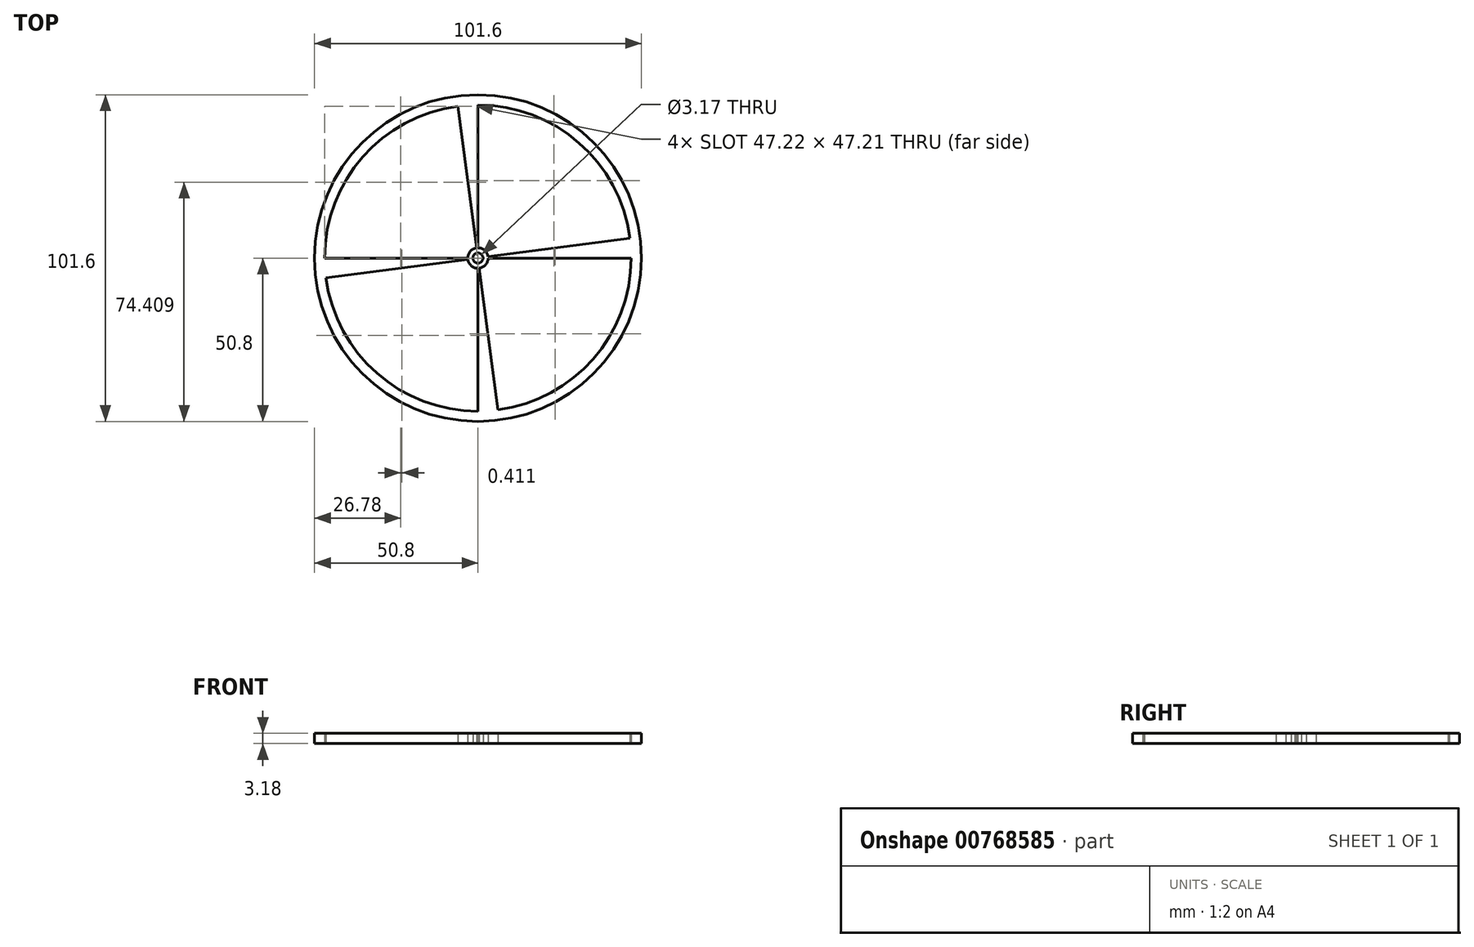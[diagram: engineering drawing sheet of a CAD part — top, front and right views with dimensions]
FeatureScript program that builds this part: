
annotation { "Feature Type Name" : "Feature", "Feature Type Description" : "" }
export const myFeature = defineFeature(function(context is Context, id is Id, definition is map)
    precondition{}
    {
        {
            var Q0;
            Q0=qCreatedBy(makeId("Top.planeOp"),FACE);
            var sketch = newSketch(context, id + "F0", { "sketchPlane" : qUnion([Q0])});
            skCircle(sketch, "E0", {"center": v(0, 0) * mm, "radius": 1.59 * mm});
            skCircle(sketch, "E1", {"center": v(0, 0) * mm, "radius": 50.8 * mm});
            skLineSegment(sketch, "E2", {"start": v(0, 0) * mm, "end": v(0, 50.8) * mm});
            skLineSegment(sketch, "E3", {"start": v(0, 0) * mm, "end": v(0, -50.8) * mm});
            skLineSegment(sketch, "E4", {"start": v(0, 0) * mm, "end": v(50.8, 0) * mm});
            skLineSegment(sketch, "E5", {"start": v(0, 0) * mm, "end": v(-50.8, 0) * mm});
            skLineSegment(sketch, "E6", {"start": v(0, 0) * mm, "end": v(-6.63, 50.37) * mm});
            skLineSegment(sketch, "E7", {"start": v(0, 0) * mm, "end": v(6.63, -50.37) * mm});
            skLineSegment(sketch, "E8", {"start": v(0, 0) * mm, "end": v(-50.37, -6.63) * mm});
            skLineSegment(sketch, "E9", {"start": v(0, 0) * mm, "end": v(50.37, 6.63) * mm});
            skCircle(sketch, "E10", {"center": v(0, 0) * mm, "radius": 47.63 * mm});
            skCircle(sketch, "E11", {"center": v(0, 0) * mm, "radius": 3.18 * mm});
            skSolve(sketch);
        }
        {
            var Q0;
            {var subQ0=sQuery(id+"F0.wireOp",EDGE,"E5");var subQ1=sQuery(id+"F0.wireOp",EDGE,"E1");var subQ2=makeQuery(id+"F0.imprint","INTERSECT",VERTEX,{"derivedFrom":[subQ1,subQ0]});Q0=makeQuery(id+"F0.imprint","IMPRINT",FACE,{"disambiguationData":[TD([[makeQuery(id+"F0.imprint","IMPRINT",EDGE,{"disambiguationData":[TD([[subQ2,1.0]])],"derivedFrom":subQ1}),1.0]])]});}
            var Q1;
            {var subQ0=sQuery(id+"F0.wireOp",EDGE,"E5");var subQ1=sQuery(id+"F0.wireOp",EDGE,"E1");var subQ2=makeQuery(id+"F0.imprint","INTERSECT",VERTEX,{"derivedFrom":[subQ1,subQ0]});Q1=makeQuery(id+"F0.imprint","IMPRINT",FACE,{"disambiguationData":[TD([[makeQuery(id+"F0.imprint","IMPRINT",EDGE,{"disambiguationData":[TD([[subQ2,-1.0]])],"derivedFrom":subQ1}),1.0]])]});}
            var Q2;
            {var subQ0=sQuery(id+"F0.wireOp",EDGE,"E3");var subQ1=sQuery(id+"F0.wireOp",EDGE,"E1");var subQ2=makeQuery(id+"F0.imprint","INTERSECT",VERTEX,{"derivedFrom":[subQ1,subQ0]});Q2=makeQuery(id+"F0.imprint","IMPRINT",FACE,{"disambiguationData":[TD([[makeQuery(id+"F0.imprint","IMPRINT",EDGE,{"disambiguationData":[TD([[subQ2,1.0]])],"derivedFrom":subQ1}),1.0]])]});}
            var Q3;
            {var subQ0=sQuery(id+"F0.wireOp",EDGE,"E4");var subQ1=sQuery(id+"F0.wireOp",EDGE,"E1");var subQ2=makeQuery(id+"F0.imprint","INTERSECT",VERTEX,{"derivedFrom":[subQ1,subQ0]});Q3=makeQuery(id+"F0.imprint","IMPRINT",FACE,{"disambiguationData":[TD([[makeQuery(id+"F0.imprint","IMPRINT",EDGE,{"disambiguationData":[TD([[subQ2,1.0]])],"derivedFrom":subQ1}),1.0]])]});}
            var Q4;
            {var subQ0=sQuery(id+"F0.wireOp",EDGE,"E2");var subQ1=sQuery(id+"F0.wireOp",EDGE,"E1");var subQ2=makeQuery(id+"F0.imprint","INTERSECT",VERTEX,{"derivedFrom":[subQ1,subQ0]});Q4=makeQuery(id+"F0.imprint","IMPRINT",FACE,{"disambiguationData":[TD([[makeQuery(id+"F0.imprint","IMPRINT",EDGE,{"disambiguationData":[TD([[subQ2,1.0]])],"derivedFrom":subQ1}),1.0]])]});}
            var Q5;
            {var subQ0=sQuery(id+"F0.wireOp",EDGE,"E2");var subQ1=sQuery(id+"F0.wireOp",EDGE,"E1");var subQ2=makeQuery(id+"F0.imprint","INTERSECT",VERTEX,{"derivedFrom":[subQ1,subQ0]});Q5=makeQuery(id+"F0.imprint","IMPRINT",FACE,{"disambiguationData":[TD([[makeQuery(id+"F0.imprint","IMPRINT",EDGE,{"disambiguationData":[TD([[subQ2,-1.0]])],"derivedFrom":subQ1}),1.0]])]});}
            var Q6;
            {var subQ0=sQuery(id+"F0.wireOp",EDGE,"E4");var subQ1=sQuery(id+"F0.wireOp",EDGE,"E1");var subQ2=makeQuery(id+"F0.imprint","INTERSECT",VERTEX,{"derivedFrom":[subQ1,subQ0]});Q6=makeQuery(id+"F0.imprint","IMPRINT",FACE,{"disambiguationData":[TD([[makeQuery(id+"F0.imprint","IMPRINT",EDGE,{"disambiguationData":[TD([[subQ2,-1.0]])],"derivedFrom":subQ1}),1.0]])]});}
            var Q7;
            {var subQ0=sQuery(id+"F0.wireOp",EDGE,"E3");var subQ1=sQuery(id+"F0.wireOp",EDGE,"E1");var subQ2=makeQuery(id+"F0.imprint","INTERSECT",VERTEX,{"derivedFrom":[subQ1,subQ0]});Q7=makeQuery(id+"F0.imprint","IMPRINT",FACE,{"disambiguationData":[TD([[makeQuery(id+"F0.imprint","IMPRINT",EDGE,{"disambiguationData":[TD([[subQ2,-1.0]])],"derivedFrom":subQ1}),1.0]])]});}
            var Q8;
            {var subQ0=sQuery(id+"F0.wireOp",EDGE,"E6");var subQ1=sQuery(id+"F0.wireOp",EDGE,"E0");var subQ2=makeQuery(id+"F0.imprint","INTERSECT",VERTEX,{"derivedFrom":[subQ1,subQ0]});Q8=makeQuery(id+"F0.imprint","IMPRINT",FACE,{"disambiguationData":[TD([[makeQuery(id+"F0.imprint","IMPRINT",EDGE,{"disambiguationData":[TD([[subQ2,-1.0]])],"derivedFrom":subQ1}),-1.0]])]});}
            var Q9;
            {var subQ0=sQuery(id+"F0.wireOp",EDGE,"E5");var subQ1=sQuery(id+"F0.wireOp",EDGE,"E0");var subQ2=makeQuery(id+"F0.imprint","INTERSECT",VERTEX,{"derivedFrom":[subQ1,subQ0]});Q9=makeQuery(id+"F0.imprint","IMPRINT",FACE,{"disambiguationData":[TD([[makeQuery(id+"F0.imprint","IMPRINT",EDGE,{"disambiguationData":[TD([[subQ2,-1.0]])],"derivedFrom":subQ1}),-1.0]])]});}
            var Q10;
            {var subQ0=sQuery(id+"F0.wireOp",EDGE,"E8");var subQ1=sQuery(id+"F0.wireOp",EDGE,"E0");var subQ2=makeQuery(id+"F0.imprint","INTERSECT",VERTEX,{"derivedFrom":[subQ1,subQ0]});Q10=makeQuery(id+"F0.imprint","IMPRINT",FACE,{"disambiguationData":[TD([[makeQuery(id+"F0.imprint","IMPRINT",EDGE,{"disambiguationData":[TD([[subQ2,-1.0]])],"derivedFrom":subQ1}),-1.0]])]});}
            var Q11;
            {var subQ0=sQuery(id+"F0.wireOp",EDGE,"E3");var subQ1=sQuery(id+"F0.wireOp",EDGE,"E0");var subQ2=makeQuery(id+"F0.imprint","INTERSECT",VERTEX,{"derivedFrom":[subQ1,subQ0]});Q11=makeQuery(id+"F0.imprint","IMPRINT",FACE,{"disambiguationData":[TD([[makeQuery(id+"F0.imprint","IMPRINT",EDGE,{"disambiguationData":[TD([[subQ2,-1.0]])],"derivedFrom":subQ1}),-1.0]])]});}
            var Q12;
            {var subQ0=sQuery(id+"F0.wireOp",EDGE,"E4");var subQ1=sQuery(id+"F0.wireOp",EDGE,"E0");var subQ2=makeQuery(id+"F0.imprint","INTERSECT",VERTEX,{"derivedFrom":[subQ1,subQ0]});Q12=makeQuery(id+"F0.imprint","IMPRINT",FACE,{"disambiguationData":[TD([[makeQuery(id+"F0.imprint","IMPRINT",EDGE,{"disambiguationData":[TD([[subQ2,1.0]])],"derivedFrom":subQ1}),-1.0]])]});}
            var Q13;
            {var subQ0=sQuery(id+"F0.wireOp",EDGE,"E9");var subQ1=sQuery(id+"F0.wireOp",EDGE,"E0");var subQ2=makeQuery(id+"F0.imprint","INTERSECT",VERTEX,{"derivedFrom":[subQ1,subQ0]});Q13=makeQuery(id+"F0.imprint","IMPRINT",FACE,{"disambiguationData":[TD([[makeQuery(id+"F0.imprint","IMPRINT",EDGE,{"disambiguationData":[TD([[subQ2,1.0]])],"derivedFrom":subQ1}),-1.0]])]});}
            var Q14;
            {var subQ0=sQuery(id+"F0.wireOp",EDGE,"E9");var subQ1=sQuery(id+"F0.wireOp",EDGE,"E0");var subQ2=makeQuery(id+"F0.imprint","INTERSECT",VERTEX,{"derivedFrom":[subQ1,subQ0]});Q14=makeQuery(id+"F0.imprint","IMPRINT",FACE,{"disambiguationData":[TD([[makeQuery(id+"F0.imprint","IMPRINT",EDGE,{"disambiguationData":[TD([[subQ2,-1.0]])],"derivedFrom":subQ1}),-1.0]])]});}
            var Q15;
            {var subQ0=sQuery(id+"F0.wireOp",EDGE,"E2");var subQ1=sQuery(id+"F0.wireOp",EDGE,"E0");var subQ2=makeQuery(id+"F0.imprint","INTERSECT",VERTEX,{"derivedFrom":[subQ1,subQ0]});Q15=makeQuery(id+"F0.imprint","IMPRINT",FACE,{"disambiguationData":[TD([[makeQuery(id+"F0.imprint","IMPRINT",EDGE,{"disambiguationData":[TD([[subQ2,-1.0]])],"derivedFrom":subQ1}),-1.0]])]});}
            var Q16;
            {var subQ0=sQuery(id+"F0.wireOp",EDGE,"E11");var subQ1=sQuery(id+"F0.wireOp",EDGE,"E2");var subQ2=makeQuery(id+"F0.imprint","INTERSECT",VERTEX,{"derivedFrom":[subQ1,subQ0]});Q16=makeQuery(id+"F0.imprint","IMPRINT",FACE,{"disambiguationData":[TD([[makeQuery(id+"F0.imprint","IMPRINT",EDGE,{"disambiguationData":[TD([[subQ2,-1.0]])],"derivedFrom":subQ1}),1.0]])]});}
            var Q17;
            {var subQ0=sQuery(id+"F0.wireOp",EDGE,"E11");var subQ1=sQuery(id+"F0.wireOp",EDGE,"E5");var subQ2=makeQuery(id+"F0.imprint","INTERSECT",VERTEX,{"derivedFrom":[subQ1,subQ0]});Q17=makeQuery(id+"F0.imprint","IMPRINT",FACE,{"disambiguationData":[TD([[makeQuery(id+"F0.imprint","IMPRINT",EDGE,{"disambiguationData":[TD([[subQ2,-1.0]])],"derivedFrom":subQ1}),1.0]])]});}
            var Q18;
            {var subQ0=sQuery(id+"F0.wireOp",EDGE,"E11");var subQ1=sQuery(id+"F0.wireOp",EDGE,"E3");var subQ2=makeQuery(id+"F0.imprint","INTERSECT",VERTEX,{"derivedFrom":[subQ1,subQ0]});Q18=makeQuery(id+"F0.imprint","IMPRINT",FACE,{"disambiguationData":[TD([[makeQuery(id+"F0.imprint","IMPRINT",EDGE,{"disambiguationData":[TD([[subQ2,-1.0]])],"derivedFrom":subQ1}),1.0]])]});}
            var Q19;
            {var subQ0=sQuery(id+"F0.wireOp",EDGE,"E11");var subQ1=sQuery(id+"F0.wireOp",EDGE,"E4");var subQ2=makeQuery(id+"F0.imprint","INTERSECT",VERTEX,{"derivedFrom":[subQ1,subQ0]});Q19=makeQuery(id+"F0.imprint","IMPRINT",FACE,{"disambiguationData":[TD([[makeQuery(id+"F0.imprint","IMPRINT",EDGE,{"disambiguationData":[TD([[subQ2,-1.0]])],"derivedFrom":subQ1}),1.0]])]});}
            extrude(context, id + "F1", {"entities" : qUnion([Q0, Q1, Q2, Q3, Q4, Q5, Q6, Q7, Q8, Q9, Q10, Q11, Q12, Q13, Q14, Q15, Q16, Q17, Q18, Q19]), "depth" : 3.17 * mm, "offsetDistance" : 25.4 * mm});
        }
    });
